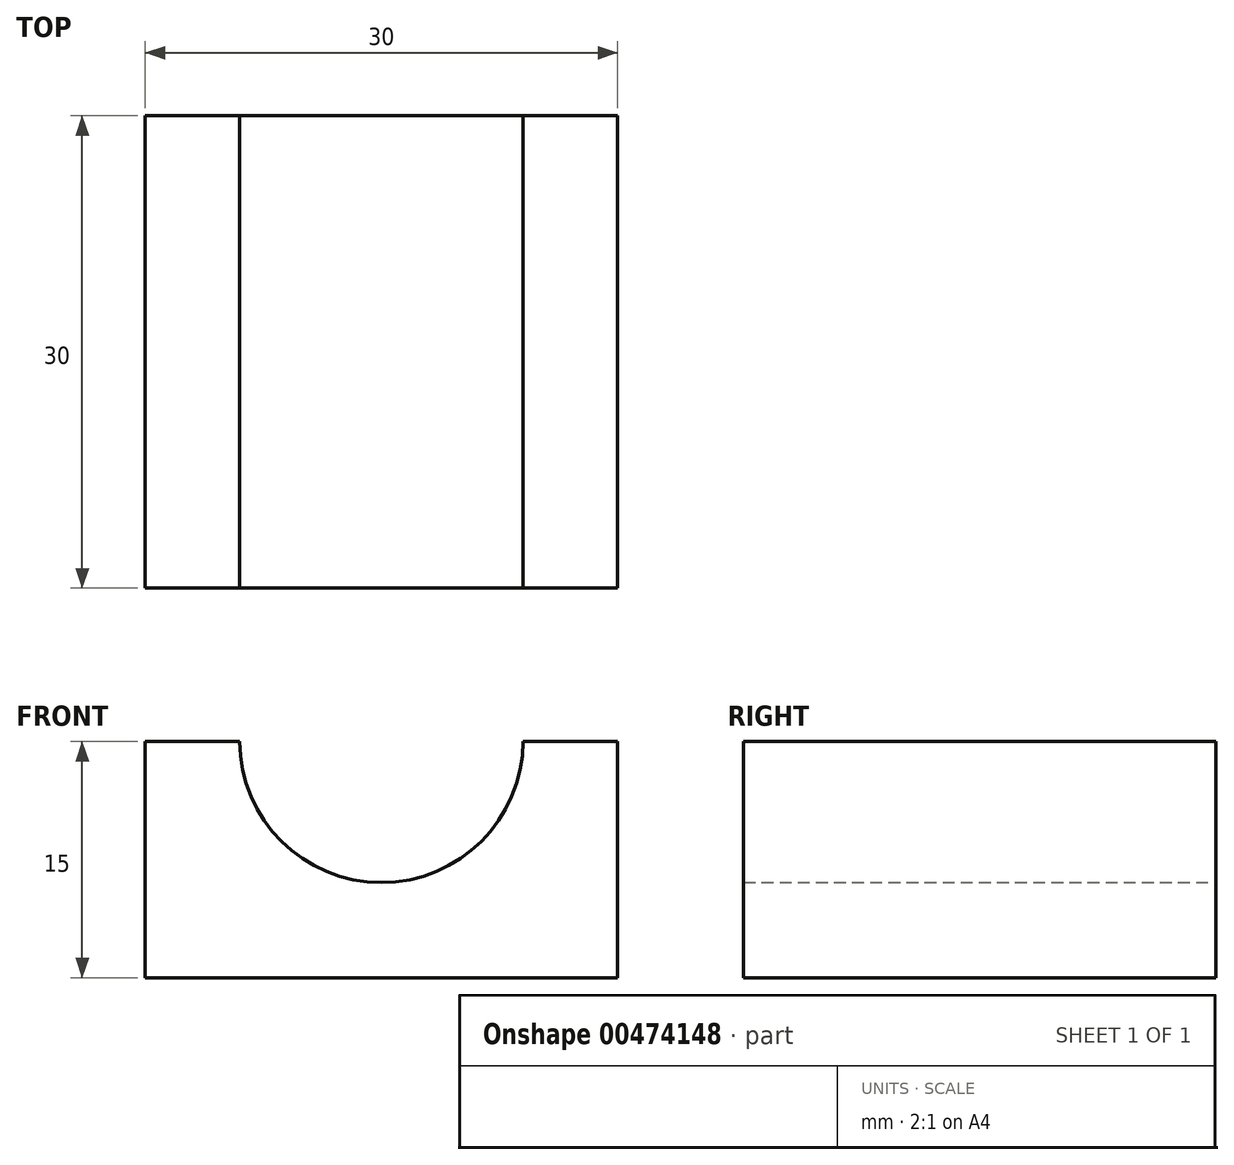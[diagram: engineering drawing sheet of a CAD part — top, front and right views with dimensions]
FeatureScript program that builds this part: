
annotation { "Feature Type Name" : "Feature", "Feature Type Description" : "" }
export const myFeature = defineFeature(function(context is Context, id is Id, definition is map)
    precondition{}
    {
        {
            var Q0;
            Q0=qCreatedBy(makeId("Front.planeOp"),FACE);
            var sketch = newSketch(context, id + "F0", { "sketchPlane" : qUnion([Q0])});
            skLineSegment(sketch, "E0.bottom", {"start": v(0.19, 30) * mm, "end": v(30.19, 30) * mm});
            skLineSegment(sketch, "E0.top", {"start": v(0.19, 0) * mm, "end": v(30.19, 0) * mm});
            skLineSegment(sketch, "E0.left", {"start": v(0.19, 30) * mm, "end": v(0.19, 0) * mm});
            skLineSegment(sketch, "E0.right", {"start": v(30.19, 30) * mm, "end": v(30.19, 0) * mm});
            skCircle(sketch, "E1", {"center": v(15.19, 15.05) * mm, "radius": 9 * mm});
            skSolve(sketch);
        }
        {
            var Q0;
            Q0 = qSketchRegion(id + "F0", true);
            extrude(context, id + "F1", {"entities" : qUnion([Q0]), "depth" : 30 * mm});
        }
        {
            var Q0;
            Q0=makeQuery(id+"F1.opExtrude","SWEPT_FACE",FACE,{"disambiguationData":[OSD([sQuery(id+"F0.wireOp",EDGE,"E0.bottom")])]});
            extrude(context, id + "F2", {"entities" : qUnion([Q0]), "operationType" : NewBodyOperationType.REMOVE, "oppositeDirection" : true, "depth" : 15 * mm});
        }
    });
